# Revit family: IS_ILifeB_T5217_BIM_NL
name_source: partatom
category: Plumbing Fixtures
units: mm (PartAtom-declared; Revit-internal decimal feet)

## family parameters
Always vertical = No
Cut with Voids When Loaded = No
OmniClass Number = 23.45.05.21.11.11
OmniClass Title = Water Operated Water Closets
Part Type = Normal
Room Calculation Point = No
Round Connector Dimension = Use Diameter
Shared = No
Work Plane-Based = No

## types (2) — shared parameters
Accessories = https://www.idealstandard.nl
Afmetingen = 361 x 542 x 377 mm
AfstandsEenheid = Millimeter
AreaMeasurement = Internal
AreaUnits = millimetres
AssetType = Fixed
Auteur = Ideal Standard
BIMObjectName = IS_IdealStandard_WCpans_i.lifeB_T5217
BIMobject category = Toilets
BIMobject category code = toilets
BIMobject main category = Sanitary
BIMobject main category code = sanitary
Beschrijvinggarantie = Herstellergarantie
BimObjectNaam = IS_IdealStandard_WCpans_i.lifeB_T5217
Brand = Ideal Standard
Brand url = http://www.idealstandard.nl
Breedte = 361.039246
Category = Sanitary
Classification = WC Pans
ConnectionType = Plumbing
CurrencyUnit = €
CurrentRevision = 1
Date of publishing = 22/07/2022
Diepte = 542 mm  [stored 1.77822 ft]
DurationUnit = Years
DuurEenheid = Jahre
Edition number = 1
ElementType = Fixed
ExpectedLife = 99
GarantieduurInstallatie = https://www.idealstandard.nl
Garantieonderdelen = https://www.idealstandard.nl
Garantieunits = Jahre
GemaaktOp = 22/07/2022
Help = https://www.idealstandard.nl
Hoogte = 376.993075245148
Hulp = https://www.idealstandard.nl
IFC Classification = Sanitary Terminal
IfcExportAs = IfcSanitaryTerminalType
IfcExportType = WCSEAT
Installatieinstructies = https://www.idealstandard.nl
Installation instructions = https://www.idealstandard.nl
InstallationInstructions = https://www.idealstandard.nl
Lengte = 542 mm  [stored 1.77822 ft]
LinearUnits = millimetres
MaintenanceInformation = https://www.idealstandard.nl
Manufacturer = Ideal Standard
Manufacturer name = Ideal Standard
ManufacturerURL = https://www.idealstandard.nl
Materiaal = Acryl-
Material = Fireclay
Material main = Fireclay
Merk = Ideal Standard
ModelReference = Ideal Standard i.life B, wallhung bowl, RimLS+, hidden fixation, Easyfix+, incl. dedicated seat wrapover, softclose
NBS Reference Code = 45-35-70/384
NBS Reference Description = WC pans
Name = WCpans_i.lifeB_T5217_IdealStandard
NettWeight = 22.5
Nettogewicht = 22.5
NominalDepth = 542 mm  [stored 1.77822 ft]
NominalHeight = 377 mm
NominalLength = 542 mm  [stored 1.77822 ft]
NominalWidth = 361 mm
OmniClass Code = 23-31 19 00
OmniClass Description = Toilets
OppervlakteEenheid = Millimeter
PanMaterial = Finefire Clay
PanMounting = Wall Hung
PredefinedType = WC Pans
Product Guid = 1a506f23-7abb-4e24-81aa-ca660b40d9c5
Product SKU = T5217
Product certification = https://www.idealstandard.nl
Product data url = https://bimobject.com
Product family = I.Life B
Product group = Sanitary
Product name = I.Life b, wallhung bowl, Easyfix+ with softclose seat
Product url = https://www.idealstandard.nl
ProductInformation = https://www.idealstandard.nl
Productinformatie = https://www.idealstandard.nl
QR code = http://bimobject.com
Revisie = 1
SeatColor = White
SeatHasCover = No
SeatMaterial = Acrylic
SeatType = Soft Close
Shape = sculptured
Size = 361 x 542 x 377 mm
Space = Internal
SpareParts = https://www.idealstandard.nl
Technical description = https://www.idealstandard.nl
Telefoonnummer = 077 355 08 08
Toepassing = WC Pans
ToiletPanType = Wall -Hung WC Bowl
ToiletType = Wall -Hung WC Bowl
Typeconnectie = Installation
UNSPSC Code = 301815
URL = https://www.idealstandard.nl
Uniclass 2015 Code = Pr_40_20_93_95
Uniclass 2015 Name = WC seats and covers
Uniclass2015Beschrijving = WC seats and covers
Uniclass2015Code = Pr_40_20_93_95
Uniclass2015Referentie = Pr_40_20_93_95
Uniclass2015Title = WC seats and covers
Uniclass2015Version = v1.26
Urlproducent = https://www.idealstandard.nl
ValutaEenheid = Euro
Versie = 1
Version = 1
Verwachtelevensduur = 2
VolumeUnits = Liters
Volumeunits = Liter
Vorm = geformt
WRASURL = https://www.wrasapprovals.co.uk
WarrantyDescription = manufacturer warranty
WarrantyDurationUnit = Years
Weight Net (Kg) = 22.5
Wisselstukken = https://www.idealstandard.nl
Youtube clip = https://www.youtube.com
zero-valued in all types: BrutoGewicht, Cost, Default Elevation, Vervangingskosten

## per-type parameters (varying)
| type | Afwerking | Artikelnummer | Artikelomschrijving | Artikelreferentie | BarCode | Barcode | Color | Description | Eigenschappen | Features | Finish | GTIN code | Kleur | Kleurwc | MainColor | Model | ModelNumber | PanColor | Referentie |
| T521701 - Ideal Standard i.life B, wallhung bowl, RimLS+, hidden fixation, Easyfix+, incl. dedicated seat wrapover, softclose - White Finish | Weiß | T521701 | Ideal Standard i.life B, wandhängendes Becken, RimLS+, verdeckte Befestigung, Easyfix+, inkl. dedizierter Sitzbezug, Softclose, weiß, in Bildkarton, EU-Palette | T521701 | 8014140503293 | 8014140503293 | White | Ideal Standard i.life B, wallhung bowl, RimLS+, hidden fixation, Easyfix+, incl. dedicated seat wrapover, softclose, white, in picture carton box, EU pallet | wandhängendes Becken, RimLS+, verdeckte Befestigung, Easyfix+, inkl. dedizierter Sitzbezug, Softclose, weiß, in Bildkarton, EU-Palette | wallhung bowl, RimLS+, hidden fixation, Easyfix+, incl. dedicated seat wrapover, softclose, white, in picture carton box, EU pallet | White | 8014140503293 | Weiß | Weiß | White | T521701 | T521701 | White | Ideal Standard i.life B sandwich seat, softclose,  easy-take off push button, adjustable hinge |
| T5217HY - Ideal Standard i.life B, wallhung bowl, RimLS+, hidden fixation, Easyfix+, incl. dedicated seat wrapover, softclose - Antibacterial glaze Smartguard+ | Weiß Smartguard+ | T5217HY | Ideal Standard i.life B, wandhängendes Becken, RimLS+, verdeckte Befestigung, Easyfix+, inkl. dedizierter Sitzbezug, Softclose, antibakterielle Verglasung Smartguard+, im Karton, EU-Palette | T5217HY | 8014140514749 | 8014140514749 | white Smartguard+ | Ideal Standard i.life B, wallhung bowl, RimLS+, hidden fixation, Easyfix+, incl. dedicated seat wrapover, softclose, antibacterial glaze Smartguard+, in carton box, EU pallet | wandhängendes Becken, RimLS+, verdeckte Befestigung, Easyfix+, inkl. dedizierter Sitzbezug, Softclose, antibakterielle Verglasung Smartguard+, im Karton, EU-Palette | wallhung bowl, RimLS+, hidden fixation, Easyfix+, incl. dedicated seat wrapover, softclose, antibacterial glaze Smartguard+, in carton box, EU pallet | white Smartguard+ | 8014140514749 | Weiß Smartguard+ | Weiß Smartguard+ | white Smartguard+ | T5217HY | T5217HY | white Smartguard+ | Ideal Standard i.life B, wallhung bowl, RimLS+, hidden fixation, Easyfix+, incl. dedicated seat wrapover, softclose |

note: [stored X ft] marks values corroborated as IEEE doubles in the binary element streams (Revit-internal decimal feet)

## geometry (parser evidence)
native form markers: Blend x2, Sweep x3
no freeform markers — native parametric forms only
